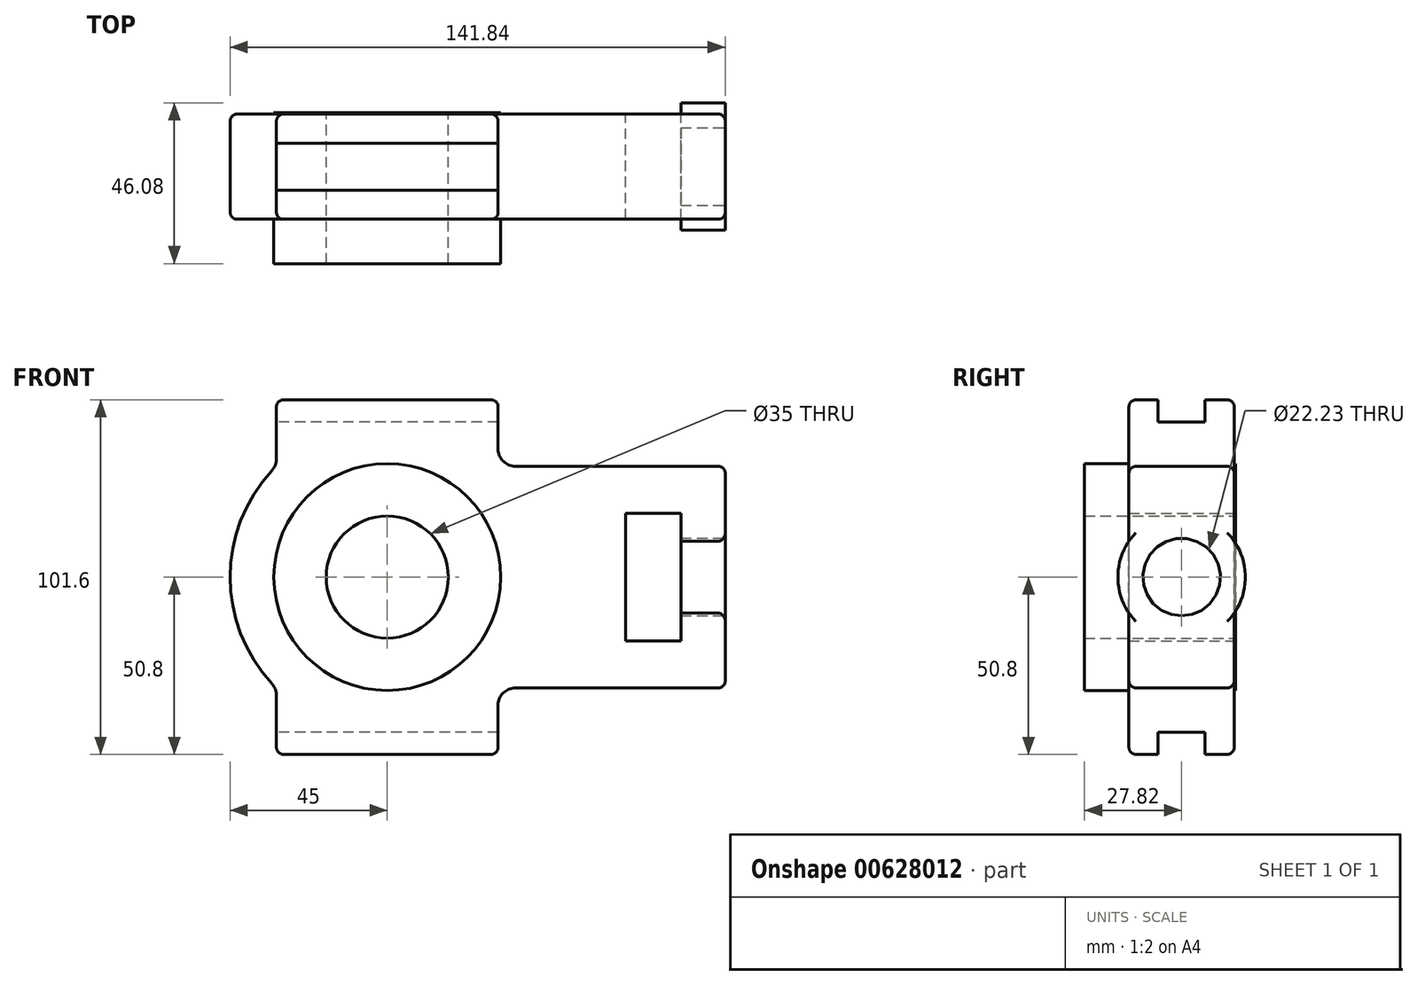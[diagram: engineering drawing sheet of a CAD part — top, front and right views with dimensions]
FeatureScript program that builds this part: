
annotation { "Feature Type Name" : "Feature", "Feature Type Description" : "" }
export const myFeature = defineFeature(function(context is Context, id is Id, definition is map)
    precondition{}
    {
        {
            var Q0;
            Q0=qCreatedBy(makeId("Front.planeOp"),FACE);
            var sketch = newSketch(context, id + "F0", { "sketchPlane" : qUnion([Q0])});
            skLineSegment(sketch, "E0.bottom", {"start": v(-29.75, 50.8) * mm, "end": v(29.75, 50.8) * mm});
            skLineSegment(sketch, "E0.top", {"start": v(-29.75, -50.8) * mm, "end": v(29.75, -50.8) * mm});
            skLineSegment(sketch, "E0.left", {"start": v(-31.75, 48.8) * mm, "end": v(-31.75, 33.9) * mm});
            skLineSegment(sketch, "E0.right", {"start": v(31.75, 48.8) * mm, "end": v(31.75, 36.75) * mm});
            skPoint(sketch, "E0.middle", {"position": v(0, 0) * mm});
            skLineSegment(sketch, "E1.bottom", {"start": v(94.84, 31.75) * mm, "end": v(36.75, 31.75) * mm});
            skLineSegment(sketch, "E1.top", {"start": v(94.84, -31.75) * mm, "end": v(36.75, -31.75) * mm});
            skLineSegment(sketch, "E1.left", {"start": v(96.84, 29.75) * mm, "end": v(96.84, -29.75) * mm});
            skPoint(sketch, "E2.orphan", {"position": v(-96.84, -31.75) * mm});
            skLineSegment(sketch, "E3.bottom", {"start": v(68.26, 18.26) * mm, "end": v(84.14, 18.26) * mm});
            skLineSegment(sketch, "E3.top", {"start": v(68.26, -18.26) * mm, "end": v(84.14, -18.26) * mm});
            skLineSegment(sketch, "E3.left", {"start": v(68.26, 18.26) * mm, "end": v(68.26, -18.26) * mm});
            skLineSegment(sketch, "E3.right", {"start": v(84.14, 18.26) * mm, "end": v(84.14, -18.26) * mm});
            skPoint(sketch, "E3.middle", {"position": v(78.24, 0) * mm});
            skCircle(sketch, "E4", {"center": v(0, 0) * mm, "radius": 17.5 * mm});
            skCircle(sketch, "E5", {"center": v(0, 0) * mm, "radius": 32.5 * mm});
            skArc(sketch, "E6", {"start": v(-33.08, -30.51) * mm, "mid": v(-45, 0) * mm, "end": v(-33.07, 30.51) * mm});
            skLineSegment(sketch, "E7.trimOffspring", {"start": v(31.75, -36.75) * mm, "end": v(31.75, -48.8) * mm});
            skLineSegment(sketch, "E8.trimOffspring", {"start": v(-31.75, -33.9) * mm, "end": v(-31.75, -48.8) * mm});
            skPoint(sketch, "E9.visualSharp", {"position": v(31.75, -31.75) * mm});
            skArc(sketch, "E9.filletArc", {"start": v(36.75, -31.75) * mm, "mid": v(33.21, -33.21) * mm, "end": v(31.75, -36.75) * mm});
            skPoint(sketch, "E10.visualSharp", {"position": v(31.75, -50.8) * mm});
            skArc(sketch, "E10.filletArc", {"start": v(29.75, -50.8) * mm, "mid": v(31.16, -50.21) * mm, "end": v(31.75, -48.8) * mm});
            skPoint(sketch, "E11.visualSharp", {"position": v(-31.75, -50.8) * mm});
            skArc(sketch, "E11.filletArc", {"start": v(-31.75, -48.8) * mm, "mid": v(-31.16, -50.21) * mm, "end": v(-29.75, -50.8) * mm});
            skPoint(sketch, "E12.visualSharp", {"position": v(-31.75, -31.89) * mm});
            skArc(sketch, "E12.filletArc", {"start": v(-31.75, -33.9) * mm, "mid": v(-32.1, -32.08) * mm, "end": v(-33.08, -30.51) * mm});
            skPoint(sketch, "E13.visualSharp", {"position": v(-31.75, 31.89) * mm});
            skArc(sketch, "E13.filletArc", {"start": v(-33.07, 30.51) * mm, "mid": v(-32.1, 32.08) * mm, "end": v(-31.75, 33.9) * mm});
            skPoint(sketch, "E14.visualSharp", {"position": v(31.75, 31.75) * mm});
            skArc(sketch, "E14.filletArc", {"start": v(31.75, 36.75) * mm, "mid": v(33.21, 33.21) * mm, "end": v(36.75, 31.75) * mm});
            skPoint(sketch, "E15.visualSharp", {"position": v(96.84, 31.75) * mm});
            skArc(sketch, "E15.filletArc", {"start": v(96.84, 29.75) * mm, "mid": v(96.25, 31.16) * mm, "end": v(94.84, 31.75) * mm});
            skPoint(sketch, "E16.visualSharp", {"position": v(96.84, -31.75) * mm});
            skArc(sketch, "E16.filletArc", {"start": v(94.84, -31.75) * mm, "mid": v(96.25, -31.16) * mm, "end": v(96.84, -29.75) * mm});
            skPoint(sketch, "E17.visualSharp", {"position": v(-31.75, 50.8) * mm});
            skArc(sketch, "E17.filletArc", {"start": v(-29.75, 50.8) * mm, "mid": v(-31.16, 50.21) * mm, "end": v(-31.75, 48.8) * mm});
            skPoint(sketch, "E18.visualSharp", {"position": v(31.75, 50.8) * mm});
            skArc(sketch, "E18.filletArc", {"start": v(31.75, 48.8) * mm, "mid": v(31.16, 50.21) * mm, "end": v(29.75, 50.8) * mm});
            skLineSegment(sketch, "E19", {"start": v(84.14, 18.26) * mm, "end": v(96.84, 18.26) * mm});
            skLineSegment(sketch, "E20", {"start": v(84.14, -18.26) * mm, "end": v(96.84, -18.26) * mm});
            skLineSegment(sketch, "E21", {"start": v(84.14, 0) * mm, "end": v(96.84, 0) * mm});
            skSolve(sketch);
        }
        {
            var Q0;
            Q0=makeQuery(id+"F0.imprint","IMPRINT",FACE,{"disambiguationData":[TD([[makeQuery(id+"F0.imprint","IMPRINT",EDGE,{"derivedFrom":sQuery(id+"F0.wireOp",EDGE,"E0.bottom")}),-1.0]])]});
            var Q1;
            Q1=makeQuery(id+"F0.imprint","IMPRINT",FACE,{"disambiguationData":[TD([[makeQuery(id+"F0.imprint","IMPRINT",EDGE,{"derivedFrom":sQuery(id+"F0.wireOp",EDGE,"E3.right")}),1.0]])]});
            extrude(context, id + "F1", {"entities" : qUnion([Q0, Q1]), "endBound" : BoundingType.SYMMETRIC, "depth" : 30.16 * mm, "offsetDistance" : 25 * mm});
        }
        {
            var Q0;
            Q0=makeQuery(id+"F0.imprint","IMPRINT",FACE,{"disambiguationData":[TD([[makeQuery(id+"F0.imprint","IMPRINT",EDGE,{"derivedFrom":sQuery(id+"F0.wireOp",EDGE,"E4")}),-1.0]])]});
            extrude(context, id + "F2", {"entities" : qUnion([Q0]), "operationType" : NewBodyOperationType.ADD, "depth" : 27.82 * mm, "offsetDistance" : 25 * mm});
        }
        {
            var Q0;
            Q0=makeQuery(id+"F0.imprint","IMPRINT",FACE,{"disambiguationData":[TD([[makeQuery(id+"F0.imprint","IMPRINT",EDGE,{"derivedFrom":sQuery(id+"F0.wireOp",EDGE,"E4")}),-1.0]])]});
            extrude(context, id + "F3", {"entities" : qUnion([Q0]), "operationType" : NewBodyOperationType.ADD, "oppositeDirection" : true, "depth" : 15.5 * mm, "offsetDistance" : 25 * mm});
        }
        {
            var Q0;
            {var subQ0=sQuery(id+"F0.wireOp",EDGE,"E19");Q0=makeQuery(id+"F0.imprint","IMPRINT",FACE,{"disambiguationData":[TD([[makeQuery(id+"F0.imprint","IMPRINT",EDGE,{"derivedFrom":subQ0}),-1.0]])]});}
            var Q1;
            Q1=sQuery(id+"F0.wireOp",EDGE,"E21");
            revolve(context, id + "F4", {"entities" : qUnion([Q0]), "axis" : qUnion([Q1]), "revolveType" : RevolveType.FULL});
        }
        {
            var Q0;
            Q0=makeQuery(id+"F4.opRevolve","SWEPT_BODY",BODY,{"disambiguationData":[OSD([sQuery(id+"F0.wireOp",EDGE,"E1.left"),sQuery(id+"F0.wireOp",EDGE,"E3.right"),sQuery(id+"F0.wireOp",EDGE,"E19"),sQuery(id+"F0.wireOp",EDGE,"E21")])]});
            var Q1;
            Q1=makeQuery(id+"F1.opExtrude","SWEPT_BODY",BODY,{"disambiguationData":[OSD([sQuery(id+"F0.wireOp",EDGE,"E0.bottom"),sQuery(id+"F0.wireOp",EDGE,"E0.top"),sQuery(id+"F0.wireOp",EDGE,"E0.left"),sQuery(id+"F0.wireOp",EDGE,"E0.right"),sQuery(id+"F0.wireOp",EDGE,"E1.bottom"),sQuery(id+"F0.wireOp",EDGE,"E1.top"),sQuery(id+"F0.wireOp",EDGE,"E1.left"),sQuery(id+"F0.wireOp",EDGE,"E3.bottom"),sQuery(id+"F0.wireOp",EDGE,"E3.top"),sQuery(id+"F0.wireOp",EDGE,"E3.left"),sQuery(id+"F0.wireOp",EDGE,"E3.right"),sQuery(id+"F0.wireOp",EDGE,"E5"),sQuery(id+"F0.wireOp",EDGE,"E6"),sQuery(id+"F0.wireOp",EDGE,"E7.trimOffspring"),sQuery(id+"F0.wireOp",EDGE,"E8.trimOffspring"),sQuery(id+"F0.wireOp",EDGE,"E9.filletArc"),sQuery(id+"F0.wireOp",EDGE,"E10.filletArc"),sQuery(id+"F0.wireOp",EDGE,"E11.filletArc"),sQuery(id+"F0.wireOp",EDGE,"E12.filletArc"),sQuery(id+"F0.wireOp",EDGE,"E13.filletArc"),sQuery(id+"F0.wireOp",EDGE,"E14.filletArc"),sQuery(id+"F0.wireOp",EDGE,"E15.filletArc"),sQuery(id+"F0.wireOp",EDGE,"E16.filletArc"),sQuery(id+"F0.wireOp",EDGE,"E17.filletArc"),sQuery(id+"F0.wireOp",EDGE,"E18.filletArc")])]});
            booleanBodies(context, id + "F5", {"operationType" : BooleanOperationType.UNION, "tools" : qUnion([Q0, Q1])});
        }
        {
            var Q0;
            Q0=makeQuery(id+"F1.opExtrude","CAP_EDGE",EDGE,{"disambiguationData":[OSD([sQuery(id+"F0.wireOp",EDGE,"E1.bottom")])],"isStart":false});
            var Q1;
            Q1=makeQuery(id+"F1.opExtrude","CAP_EDGE",EDGE,{"disambiguationData":[OSD([sQuery(id+"F0.wireOp",EDGE,"E1.bottom")])],"isStart":true});
            fillet(context, id + "F6", {"entities" : qUnion([Q0, Q1]), "radius" : 2 * mm, "tangentPropagation" : true, "allowEdgeOverflow" : false});
        }
        {
            var Q0;
            {var subQ0=sQuery(id+"F0.wireOp",EDGE,"E1.left");Q0=makeQuery(id+"F5.opBoolean","MERGE",FACE,{"derivedFrom":[makeQuery(id+"F1.opExtrude","SWEPT_FACE",FACE,{"disambiguationData":[OSD([subQ0])]}),makeQuery(id+"F4.opRevolve","SWEPT_FACE",FACE,{"disambiguationData":[OSD([subQ0])]})]});}
            var sketch = newSketch(context, id + "F7", { "sketchPlane" : qUnion([Q0])});
            skLineSegment(sketch, "E22", {"start": v(0, 0) * mm, "end": v(-18.26, 0) * mm});
            skLineSegment(sketch, "E23", {"start": v(-18.26, 0) * mm, "end": v(0, 0) * mm});
            skLineSegment(sketch, "E24", {"start": v(18.26, 0) * mm, "end": v(0, 0) * mm});
            skSolve(sketch);
        }
        {
            var Q0;
            Q0=sQuery(id+"F7.wireOp",VERTEX,"E22.start");
            var Q1;
            Q1=makeQuery(id+"F4.opRevolve","SWEPT_BODY",BODY,{"disambiguationData":[OSD([sQuery(id+"F0.wireOp",EDGE,"E1.left"),sQuery(id+"F0.wireOp",EDGE,"E3.right"),sQuery(id+"F0.wireOp",EDGE,"E19"),sQuery(id+"F0.wireOp",EDGE,"E21")])]});
            hole(context, id + "F8", {"style" : HoleStyle.SIMPLE, "endStyle" : HoleEndStyle.BLIND, "holeDiameter" : 22.23 * mm, "majorDiameter" : 5 * mm, "holeDepth" : 13 * mm, "isTappedThrough" : true, "tappedDepth" : 12 * mm, "tapClearance" : 3, "startFromSketch" : true, "locations" : qUnion([Q0]), "scope" : qUnion([Q1])});
        }
        {
            var Q0;
            Q0=makeQuery(id+"F1.opExtrude","SWEPT_FACE",FACE,{"disambiguationData":[OSD([sQuery(id+"F0.wireOp",EDGE,"E0.top")])]});
            var sketch = newSketch(context, id + "F9", { "sketchPlane" : qUnion([Q0])});
            skPoint(sketch, "E25.middle", {"position": v(0, 0) * mm});
            skLineSegment(sketch, "E26.bottom", {"start": v(55.88, -6.75) * mm, "end": v(-55.88, -6.75) * mm});
            skLineSegment(sketch, "E26.top", {"start": v(55.88, 6.75) * mm, "end": v(-55.88, 6.75) * mm});
            skLineSegment(sketch, "E26.left", {"start": v(55.88, -6.75) * mm, "end": v(55.88, 6.75) * mm});
            skLineSegment(sketch, "E26.right", {"start": v(-55.88, -6.75) * mm, "end": v(-55.88, 6.75) * mm});
            skPoint(sketch, "E27.orphan", {"position": v(-29.75, 6.75) * mm});
            skPoint(sketch, "E25.right.end.orphan", {"position": v(-29.75, -6.75) * mm});
            skPoint(sketch, "E25.left.start.orphan", {"position": v(29.75, 6.75) * mm});
            skPoint(sketch, "E28.trimOffspring.end.orphan", {"position": v(29.75, -6.75) * mm});
            skSolve(sketch);
        }
        {
            var Q0;
            Q0 = qSketchRegion(id + "F9", true);
            extrude(context, id + "F10", {"entities" : qUnion([Q0]), "operationType" : NewBodyOperationType.REMOVE, "oppositeDirection" : true, "depth" : 6.35 * mm, "offsetDistance" : 25 * mm});
        }
        {
            var Q0;
            Q0=makeQuery(id+"F1.opExtrude","SWEPT_FACE",FACE,{"disambiguationData":[OSD([sQuery(id+"F0.wireOp",EDGE,"E0.bottom")])]});
            var sketch = newSketch(context, id + "F11", { "sketchPlane" : qUnion([Q0])});
            skLineSegment(sketch, "E29.bottom", {"start": v(40.46, 6.75) * mm, "end": v(-40.46, 6.75) * mm});
            skLineSegment(sketch, "E29.top", {"start": v(40.46, -6.75) * mm, "end": v(-40.46, -6.75) * mm});
            skLineSegment(sketch, "E29.left", {"start": v(40.46, 6.75) * mm, "end": v(40.46, -6.75) * mm});
            skLineSegment(sketch, "E29.right", {"start": v(-40.46, 6.75) * mm, "end": v(-40.46, -6.75) * mm});
            skPoint(sketch, "E29.middle", {"position": v(0, 0) * mm});
            skSolve(sketch);
        }
        {
            var Q0;
            Q0 = qSketchRegion(id + "F11", true);
            extrude(context, id + "F12", {"entities" : qUnion([Q0]), "operationType" : NewBodyOperationType.REMOVE, "oppositeDirection" : true, "depth" : 6.35 * mm, "offsetDistance" : 25 * mm});
        }
    });
